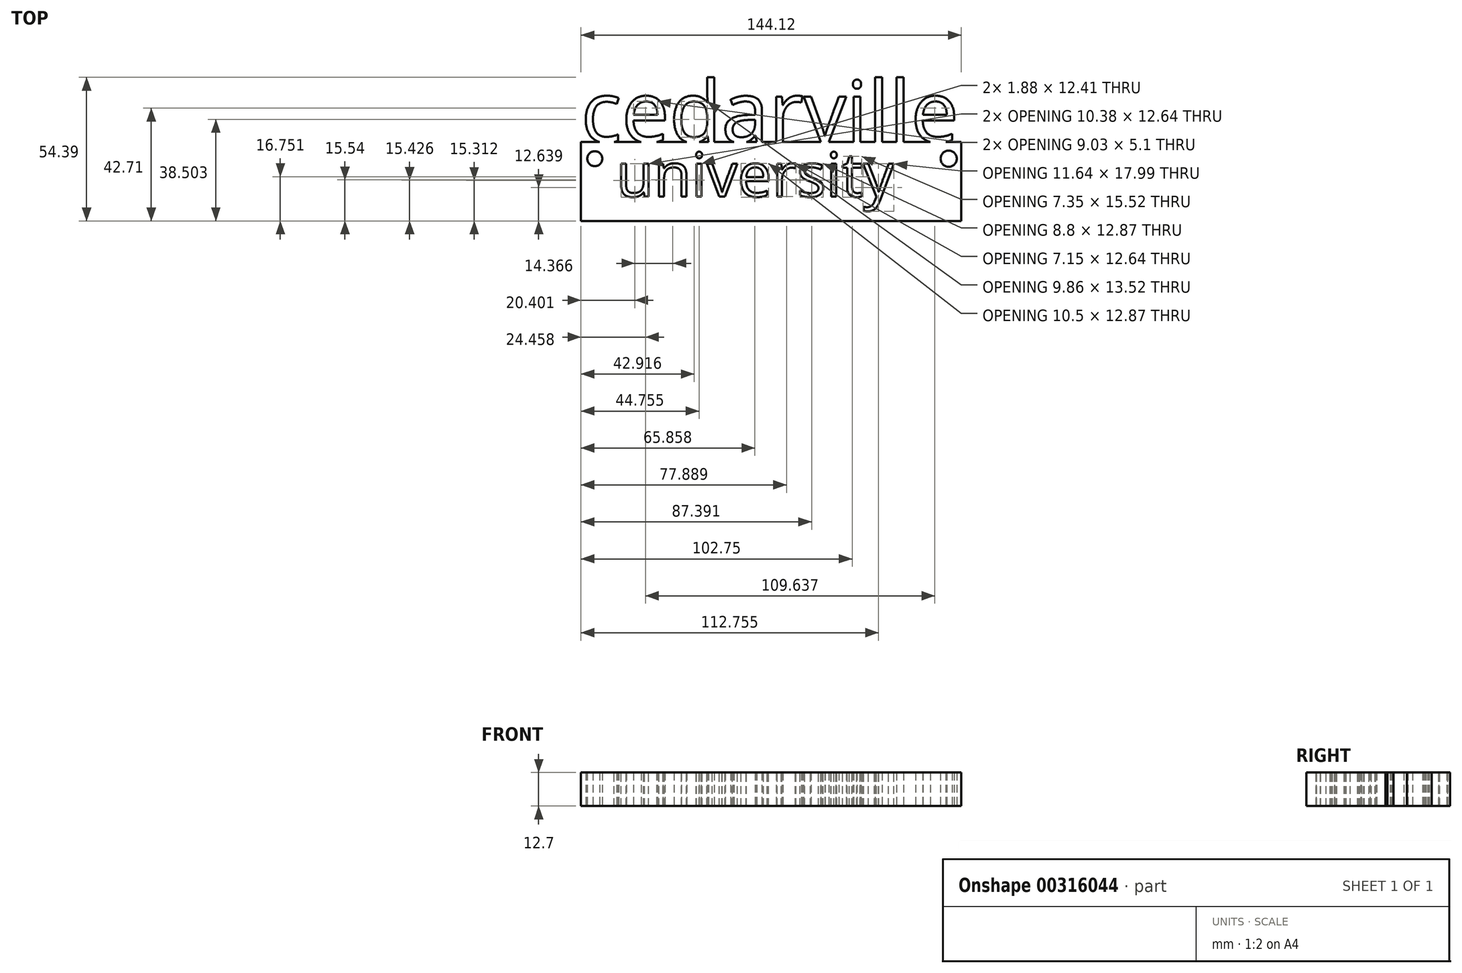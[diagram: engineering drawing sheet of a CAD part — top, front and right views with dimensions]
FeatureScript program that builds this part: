
annotation { "Feature Type Name" : "Feature", "Feature Type Description" : "" }
export const myFeature = defineFeature(function(context is Context, id is Id, definition is map)
    precondition{}
    {
        {
            var Q0;
            Q0=qCreatedBy(makeId("Top.planeOp"),FACE);
            var sketch = newSketch(context, id + "F0", { "sketchPlane" : qUnion([Q0])});
            skLineSegment(sketch, "E0.bottom", {"start": v(-71.26, 26.13) * mm, "end": v(72.86, 26.13) * mm, "construction": true});
            skLineSegment(sketch, "E1.bottom", {"start": v(-71.26, 26.13) * mm, "end": v(72.86, 26.13) * mm});
            skLineSegment(sketch, "E1.top", {"start": v(-71.26, -3.74) * mm, "end": v(72.86, -3.74) * mm});
            skLineSegment(sketch, "E1.left", {"start": v(-71.26, 26.13) * mm, "end": v(-71.26, -3.74) * mm});
            skLineSegment(sketch, "E1.right", {"start": v(72.86, 26.13) * mm, "end": v(72.86, -3.74) * mm});
            skText(sketch, "E2", { "text": "cedarville", "fontName": "OpenSans-Regular.ttf"});
            const initialGuessF0  = {"E2": [-0.07126, 0.02613, 1, 0, 0.02323]};
            skSetInitialGuess(sketch, initialGuessF0);
            skSolve(sketch);
        }
        {
            var Q0;
            Q0 = qSketchRegion(id + "F0", true);
            extrude(context, id + "F1", {"entities" : qUnion([Q0]), "depth" : 12.7 * mm});
        }
        {
            var Q0;
            Q0=qCreatedBy(makeId("Top.planeOp"),FACE);
            var sketch = newSketch(context, id + "F2", { "sketchPlane" : qUnion([Q0])});
            skCircle(sketch, "E3", {"center": v(-66.05, 19.84) * mm, "radius": 2.84 * mm});
            skCircle(sketch, "E4", {"center": v(68.07, 19.84) * mm, "radius": 3.06 * mm});
            skSolve(sketch);
        }
        {
            var Q0;
            Q0 = qSketchRegion(id + "F2", true);
            extrude(context, id + "F3", {"entities" : qUnion([Q0]), "operationType" : NewBodyOperationType.REMOVE, "depth" : 25.4 * mm});
        }
        {
            var Q0;
            Q0=makeQuery(id+"F1.opExtrude","CAP_FACE",FACE,{"disambiguationData":[OSD([sQuery(id+"F0.wireOp",EDGE,"E1.bottom"),sQuery(id+"F0.wireOp",EDGE,"E1.top"),sQuery(id+"F0.wireOp",EDGE,"E1.left"),sQuery(id+"F0.wireOp",EDGE,"E1.right"),sQuery(id+"F0.wireOp",EDGE,"E2.sketch_text.stroke-0"),sQuery(id+"F0.wireOp",EDGE,"E2.sketch_text.stroke-1"),sQuery(id+"F0.wireOp",EDGE,"E2.sketch_text.stroke-2"),sQuery(id+"F0.wireOp",EDGE,"E2.sketch_text.stroke-3"),sQuery(id+"F0.wireOp",EDGE,"E2.sketch_text.stroke-4"),sQuery(id+"F0.wireOp",EDGE,"E2.sketch_text.stroke-5"),sQuery(id+"F0.wireOp",EDGE,"E2.sketch_text.stroke-6"),sQuery(id+"F0.wireOp",EDGE,"E2.sketch_text.stroke-7"),sQuery(id+"F0.wireOp",EDGE,"E2.sketch_text.stroke-8"),sQuery(id+"F0.wireOp",EDGE,"E2.sketch_text.stroke-9"),sQuery(id+"F0.wireOp",EDGE,"E2.sketch_text.stroke-10"),sQuery(id+"F0.wireOp",EDGE,"E2.sketch_text.stroke-11"),sQuery(id+"F0.wireOp",EDGE,"E2.sketch_text.stroke-12"),sQuery(id+"F0.wireOp",EDGE,"E2.sketch_text.stroke-13"),sQuery(id+"F0.wireOp",EDGE,"E2.sketch_text.stroke-14"),sQuery(id+"F0.wireOp",EDGE,"E2.sketch_text.stroke-15"),sQuery(id+"F0.wireOp",EDGE,"E2.sketch_text.stroke-16"),sQuery(id+"F0.wireOp",EDGE,"E2.sketch_text.stroke-17"),sQuery(id+"F0.wireOp",EDGE,"E2.sketch_text.stroke-18"),sQuery(id+"F0.wireOp",EDGE,"E2.sketch_text.stroke-19"),sQuery(id+"F0.wireOp",EDGE,"E2.sketch_text.stroke-20"),sQuery(id+"F0.wireOp",EDGE,"E2.sketch_text.stroke-21"),sQuery(id+"F0.wireOp",EDGE,"E2.sketch_text.stroke-22"),sQuery(id+"F0.wireOp",EDGE,"E2.sketch_text.stroke-23"),sQuery(id+"F0.wireOp",EDGE,"E2.sketch_text.stroke-24"),sQuery(id+"F0.wireOp",EDGE,"E2.sketch_text.stroke-25"),sQuery(id+"F0.wireOp",EDGE,"E2.sketch_text.stroke-26"),sQuery(id+"F0.wireOp",EDGE,"E2.sketch_text.stroke-27"),sQuery(id+"F0.wireOp",EDGE,"E2.sketch_text.stroke-29"),sQuery(id+"F0.wireOp",EDGE,"E2.sketch_text.stroke-30"),sQuery(id+"F0.wireOp",EDGE,"E2.sketch_text.stroke-31"),sQuery(id+"F0.wireOp",EDGE,"E2.sketch_text.stroke-32"),sQuery(id+"F0.wireOp",EDGE,"E2.sketch_text.stroke-33"),sQuery(id+"F0.wireOp",EDGE,"E2.sketch_text.stroke-34"),sQuery(id+"F0.wireOp",EDGE,"E2.sketch_text.stroke-35"),sQuery(id+"F0.wireOp",EDGE,"E2.sketch_text.stroke-36"),sQuery(id+"F0.wireOp",EDGE,"E2.sketch_text.stroke-37"),sQuery(id+"F0.wireOp",EDGE,"E2.sketch_text.stroke-38"),sQuery(id+"F0.wireOp",EDGE,"E2.sketch_text.stroke-39"),sQuery(id+"F0.wireOp",EDGE,"E2.sketch_text.stroke-40"),sQuery(id+"F0.wireOp",EDGE,"E2.sketch_text.stroke-41"),sQuery(id+"F0.wireOp",EDGE,"E2.sketch_text.stroke-42"),sQuery(id+"F0.wireOp",EDGE,"E2.sketch_text.stroke-43"),sQuery(id+"F0.wireOp",EDGE,"E2.sketch_text.stroke-44"),sQuery(id+"F0.wireOp",EDGE,"E2.sketch_text.stroke-45"),sQuery(id+"F0.wireOp",EDGE,"E2.sketch_text.stroke-46"),sQuery(id+"F0.wireOp",EDGE,"E2.sketch_text.stroke-48"),sQuery(id+"F0.wireOp",EDGE,"E2.sketch_text.stroke-49"),sQuery(id+"F0.wireOp",EDGE,"E2.sketch_text.stroke-50"),sQuery(id+"F0.wireOp",EDGE,"E2.sketch_text.stroke-51"),sQuery(id+"F0.wireOp",EDGE,"E2.sketch_text.stroke-52"),sQuery(id+"F0.wireOp",EDGE,"E2.sketch_text.stroke-53"),sQuery(id+"F0.wireOp",EDGE,"E2.sketch_text.stroke-54"),sQuery(id+"F0.wireOp",EDGE,"E2.sketch_text.stroke-55"),sQuery(id+"F0.wireOp",EDGE,"E2.sketch_text.stroke-56"),sQuery(id+"F0.wireOp",EDGE,"E2.sketch_text.stroke-57"),sQuery(id+"F0.wireOp",EDGE,"E2.sketch_text.stroke-58"),sQuery(id+"F0.wireOp",EDGE,"E2.sketch_text.stroke-59"),sQuery(id+"F0.wireOp",EDGE,"E2.sketch_text.stroke-60"),sQuery(id+"F0.wireOp",EDGE,"E2.sketch_text.stroke-61"),sQuery(id+"F0.wireOp",EDGE,"E2.sketch_text.stroke-62"),sQuery(id+"F0.wireOp",EDGE,"E2.sketch_text.stroke-63"),sQuery(id+"F0.wireOp",EDGE,"E2.sketch_text.stroke-64"),sQuery(id+"F0.wireOp",EDGE,"E2.sketch_text.stroke-65"),sQuery(id+"F0.wireOp",EDGE,"E2.sketch_text.stroke-66"),sQuery(id+"F0.wireOp",EDGE,"E2.sketch_text.stroke-67"),sQuery(id+"F0.wireOp",EDGE,"E2.sketch_text.stroke-68"),sQuery(id+"F0.wireOp",EDGE,"E2.sketch_text.stroke-69"),sQuery(id+"F0.wireOp",EDGE,"E2.sketch_text.stroke-70"),sQuery(id+"F0.wireOp",EDGE,"E2.sketch_text.stroke-71"),sQuery(id+"F0.wireOp",EDGE,"E2.sketch_text.stroke-72"),sQuery(id+"F0.wireOp",EDGE,"E2.sketch_text.stroke-73"),sQuery(id+"F0.wireOp",EDGE,"E2.sketch_text.stroke-74"),sQuery(id+"F0.wireOp",EDGE,"E2.sketch_text.stroke-75"),sQuery(id+"F0.wireOp",EDGE,"E2.sketch_text.stroke-77"),sQuery(id+"F0.wireOp",EDGE,"E2.sketch_text.stroke-78"),sQuery(id+"F0.wireOp",EDGE,"E2.sketch_text.stroke-79"),sQuery(id+"F0.wireOp",EDGE,"E2.sketch_text.stroke-80"),sQuery(id+"F0.wireOp",EDGE,"E2.sketch_text.stroke-81"),sQuery(id+"F0.wireOp",EDGE,"E2.sketch_text.stroke-82"),sQuery(id+"F0.wireOp",EDGE,"E2.sketch_text.stroke-83"),sQuery(id+"F0.wireOp",EDGE,"E2.sketch_text.stroke-84"),sQuery(id+"F0.wireOp",EDGE,"E2.sketch_text.stroke-85"),sQuery(id+"F0.wireOp",EDGE,"E2.sketch_text.stroke-86"),sQuery(id+"F0.wireOp",EDGE,"E2.sketch_text.stroke-87"),sQuery(id+"F0.wireOp",EDGE,"E2.sketch_text.stroke-88"),sQuery(id+"F0.wireOp",EDGE,"E2.sketch_text.stroke-89"),sQuery(id+"F0.wireOp",EDGE,"E2.sketch_text.stroke-90"),sQuery(id+"F0.wireOp",EDGE,"E2.sketch_text.stroke-92"),sQuery(id+"F0.wireOp",EDGE,"E2.sketch_text.stroke-93"),sQuery(id+"F0.wireOp",EDGE,"E2.sketch_text.stroke-94"),sQuery(id+"F0.wireOp",EDGE,"E2.sketch_text.stroke-95"),sQuery(id+"F0.wireOp",EDGE,"E2.sketch_text.stroke-96"),sQuery(id+"F0.wireOp",EDGE,"E2.sketch_text.stroke-97"),sQuery(id+"F0.wireOp",EDGE,"E2.sketch_text.stroke-98"),sQuery(id+"F0.wireOp",EDGE,"E2.sketch_text.stroke-99"),sQuery(id+"F0.wireOp",EDGE,"E2.sketch_text.stroke-100"),sQuery(id+"F0.wireOp",EDGE,"E2.sketch_text.stroke-101"),sQuery(id+"F0.wireOp",EDGE,"E2.sketch_text.stroke-102"),sQuery(id+"F0.wireOp",EDGE,"E2.sketch_text.stroke-103"),sQuery(id+"F0.wireOp",EDGE,"E2.sketch_text.stroke-104"),sQuery(id+"F0.wireOp",EDGE,"E2.sketch_text.stroke-105"),sQuery(id+"F0.wireOp",EDGE,"E2.sketch_text.stroke-106"),sQuery(id+"F0.wireOp",EDGE,"E2.sketch_text.stroke-109"),sQuery(id+"F0.wireOp",EDGE,"E2.sketch_text.stroke-110"),sQuery(id+"F0.wireOp",EDGE,"E2.sketch_text.stroke-111"),sQuery(id+"F0.wireOp",EDGE,"E2.sketch_text.stroke-121"),sQuery(id+"F0.wireOp",EDGE,"E2.sketch_text.stroke-122"),sQuery(id+"F0.wireOp",EDGE,"E2.sketch_text.stroke-123"),sQuery(id+"F0.wireOp",EDGE,"E2.sketch_text.stroke-125"),sQuery(id+"F0.wireOp",EDGE,"E2.sketch_text.stroke-126"),sQuery(id+"F0.wireOp",EDGE,"E2.sketch_text.stroke-127"),sQuery(id+"F0.wireOp",EDGE,"E2.sketch_text.stroke-128"),sQuery(id+"F0.wireOp",EDGE,"E2.sketch_text.stroke-129"),sQuery(id+"F0.wireOp",EDGE,"E2.sketch_text.stroke-130"),sQuery(id+"F0.wireOp",EDGE,"E2.sketch_text.stroke-131"),sQuery(id+"F0.wireOp",EDGE,"E2.sketch_text.stroke-132"),sQuery(id+"F0.wireOp",EDGE,"E2.sketch_text.stroke-133"),sQuery(id+"F0.wireOp",EDGE,"E2.sketch_text.stroke-134"),sQuery(id+"F0.wireOp",EDGE,"E2.sketch_text.stroke-135"),sQuery(id+"F0.wireOp",EDGE,"E2.sketch_text.stroke-136"),sQuery(id+"F0.wireOp",EDGE,"E2.sketch_text.stroke-137"),sQuery(id+"F0.wireOp",EDGE,"E2.sketch_text.stroke-138"),sQuery(id+"F0.wireOp",EDGE,"E2.sketch_text.stroke-139"),sQuery(id+"F0.wireOp",EDGE,"E2.sketch_text.stroke-140"),sQuery(id+"F0.wireOp",EDGE,"E2.sketch_text.stroke-142"),sQuery(id+"F0.wireOp",EDGE,"E2.sketch_text.stroke-143"),sQuery(id+"F0.wireOp",EDGE,"E2.sketch_text.stroke-144"),sQuery(id+"F0.wireOp",EDGE,"E2.sketch_text.stroke-145"),sQuery(id+"F0.wireOp",EDGE,"E2.sketch_text.stroke-146")])],"isStart":false});
            var sketch = newSketch(context, id + "F4", { "sketchPlane" : qUnion([Q0])});
            skText(sketch, "E5", { "text": "university", "fontName": "OpenSans-Regular.ttf"});
            const initialGuessF4  = {"E5": [-0.05791, 0.00548, 1, 0, 0.0167]};
            skSetInitialGuess(sketch, initialGuessF4);
            skSolve(sketch);
        }
        {
            var Q0;
            Q0 = qSketchRegion(id + "F4", true);
            extrude(context, id + "F5", {"entities" : qUnion([Q0]), "operationType" : NewBodyOperationType.REMOVE, "oppositeDirection" : true, "depth" : 72.64 * mm});
        }
    });
